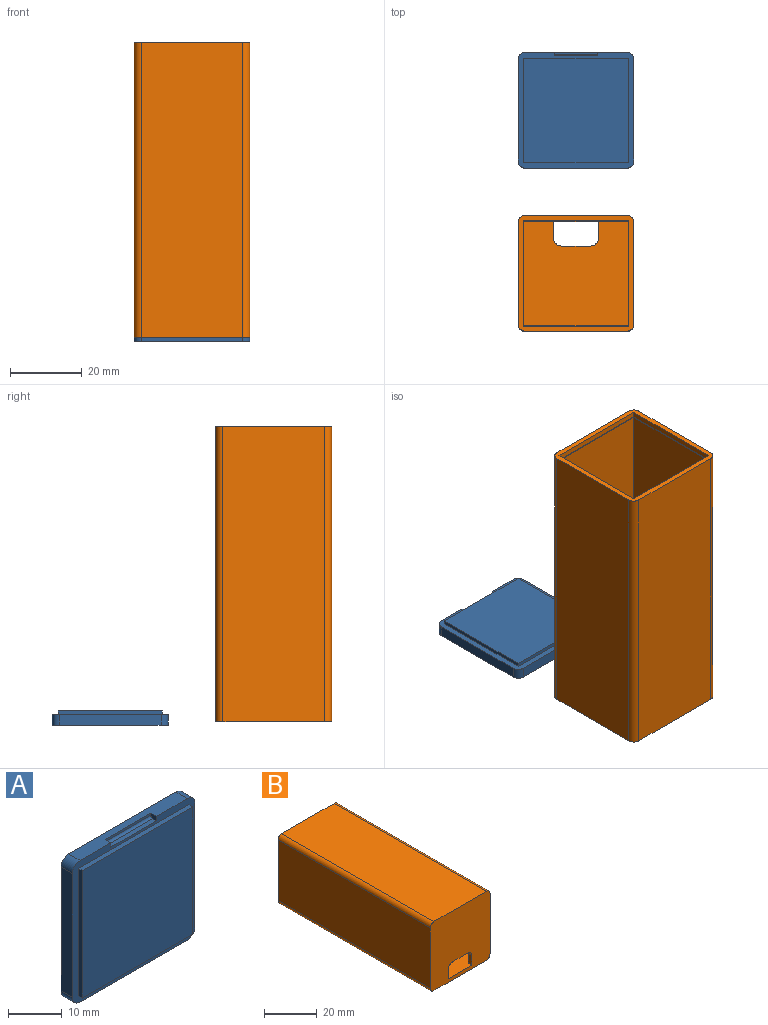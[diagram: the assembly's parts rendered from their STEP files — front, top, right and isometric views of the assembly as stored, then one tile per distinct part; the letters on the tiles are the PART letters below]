
ASSEMBLY  parts=2 mates=1
PART A: 20 faces, bbox 32.2x4x32.2 mm
  f0: plane 28.2x3mm, normal (0,0,1), area 66.6mm2, adj f1,f7,f8,f9,f15,f16,f17
  f1: cylinder r=2mm len=3mm, axis (0,-1,0), area 9.4mm2, adj f0,f2,f8,f9
  f2: plane 28.2x3mm, normal (1,0,0), area 84.6mm2, adj f1,f3,f8,f9
  f3: cylinder r=2mm len=3mm, axis (0,-1,0), area 9.4mm2, adj f2,f4,f8,f9
  f4: plane 28.2x3mm, normal (0,0,-1), area 84.6mm2, adj f3,f5,f8,f9
  f5: cylinder r=2mm len=3mm, axis (0,-1,0), area 9.4mm2, adj f4,f6,f8,f9
  f6: plane 28.2x3mm, normal (-1,0,0), area 84.6mm2, adj f5,f7,f8,f9
  f7: cylinder r=2mm len=3mm, axis (0,-1,0), area 9.4mm2, adj f0,f6,f8,f9
  f8: plane 32.2x32.2mm, normal (0,1,0), area 1033.4mm2, adj f0,f1,f2,f3,f4,f5,f6,f7
  f9: plane 32.2x32.2mm, normal (0,-1,0), area 180.4mm2, adj f0,f1,f2,f3,f4,f5,f6,f7
  f10: plane 29x1mm, normal (1,0,0), area 29mm2, adj f9,f11,f13,f14
  f11: plane 29x1mm, normal (0,0,1), area 29mm2, adj f9,f10,f12,f14
  f12: plane 29x1mm, normal (-1,0,0), area 29mm2, adj f9,f11,f13,f14
  f13: plane 29x1mm, normal (0,0,-1), area 29mm2, adj f9,f10,f12,f14
  f14: plane 29x29mm, normal (0,-1,0), area 841mm2, adj f10,f11,f12,f13
  f15: plane 1.5x1mm, normal (1,0,0), area 1.4mm2, adj f0,f9,f17,f18,f19
  f16: plane 1.5x1mm, normal (-1,0,0), area 1.4mm2, adj f0,f9,f17,f18,f19
  f17: plane 12x0.5mm, normal (0,-1,0), area 6mm2, adj f0,f15,f16,f19
  f18: plane 12x1mm, normal (0,0,1), area 12mm2, adj f9,f15,f16,f19
  f19: cylinder r=0.5mm len=12mm, axis (-1,0,0), area 9.4mm2, adj f15,f16,f17,f18
PART B: 25 faces, bbox 32.2x82x32.2 mm
  f0: plane 82x28.2mm, normal (0,0,1), area 2312.4mm2, adj f1,f11,f12,f18
  f1: cylinder r=2mm len=82mm, axis (0,-1,0), area 257.6mm2, adj f0,f2,f12,f18
  f2: plane 82x28.2mm, normal (-1,0,0), area 2312.4mm2, adj f1,f3,f12,f18
  f3: cylinder r=2mm len=82mm, axis (0,-1,0), area 257.6mm2, adj f2,f4,f12,f18
  f4: plane 82x28.2mm, normal (0,0,-1), area 2312.4mm2, adj f3,f5,f12,f18
  f5: cylinder r=2mm len=82mm, axis (0,-1,0), area 257.6mm2, adj f4,f6,f12,f18
  f6: plane 82x28.2mm, normal (1,0,0), area 2312.4mm2, adj f5,f11,f12,f18
  f7: plane 80.5x29mm, normal (0,0,1), area 2301.7mm2, adj f8,f10,f13,f17,f18,f19,f20
  f8: plane 78.5x29mm, normal (1,0,0), area 2276.5mm2, adj f7,f9,f19,f20
  f9: plane 78.5x29mm, normal (0,0,-1), area 2276.5mm2, adj f8,f10,f19,f20
  f10: plane 78.5x29mm, normal (-1,0,0), area 2276.5mm2, adj f7,f9,f19,f20
  f11: cylinder r=2mm len=82mm, axis (0,-1,0), area 257.6mm2, adj f0,f6,f12,f18
  f12: plane 32.2x32.2mm, normal (0,1,0), area 169mm2, adj f0,f1,f2,f3,f4,f5,f6,f11
  f13: plane 4.5x2mm, normal (1,0,0), area 9mm2, adj f7,f14,f18,f19
  f14: cylinder r=2.3mm len=2.3mm, axis (0,1,0), area 7.2mm2, adj f13,f15,f18,f19
  f15: plane 8x2mm, normal (0,0,-1), area 16mm2, adj f14,f16,f18,f19
  f16: cylinder r=2.3mm len=2.3mm, axis (0,1,0), area 7.2mm2, adj f15,f17,f18,f19
  f17: plane 4.5x2mm, normal (-1,0,0), area 9mm2, adj f7,f16,f18,f19
  f18: plane 32.2x32.2mm, normal (0,-1,0), area 950mm2, adj f0,f1,f2,f3,f4,f5,f6,f7
  f19: plane 29x29mm, normal (0,1,0), area 757.6mm2, adj f7,f8,f9,f10,f13,f14,f15,f16
  f20: plane 29.4x29.4mm, normal (0,1,0), area 23.4mm2, adj f7,f8,f9,f10,f21,f22,f23,f24
  f21: plane 29.4x1.5mm, normal (1,0,0), area 44.1mm2, adj f12,f20,f22,f24
  f22: plane 29.4x1.5mm, normal (0,0,1), area 44.1mm2, adj f12,f20,f21,f23
  f23: plane 29.4x1.5mm, normal (-1,0,0), area 44.1mm2, adj f12,f20,f22,f24
  f24: plane 29.4x1.5mm, normal (0,0,-1), area 44.1mm2, adj f12,f20,f21,f23
PLACE A rot(axis=(-1,0,0),90deg) t=(-22.24,10.44,15.78)mm
PLACE B rot(axis=(1,0,0),90deg) t=(-22.24,-5.98,-64.22)mm
MATE parallel A.f8 <-> B.f18  axis (0,0,-1) through (-7.74,24.94,-67.22)mm
